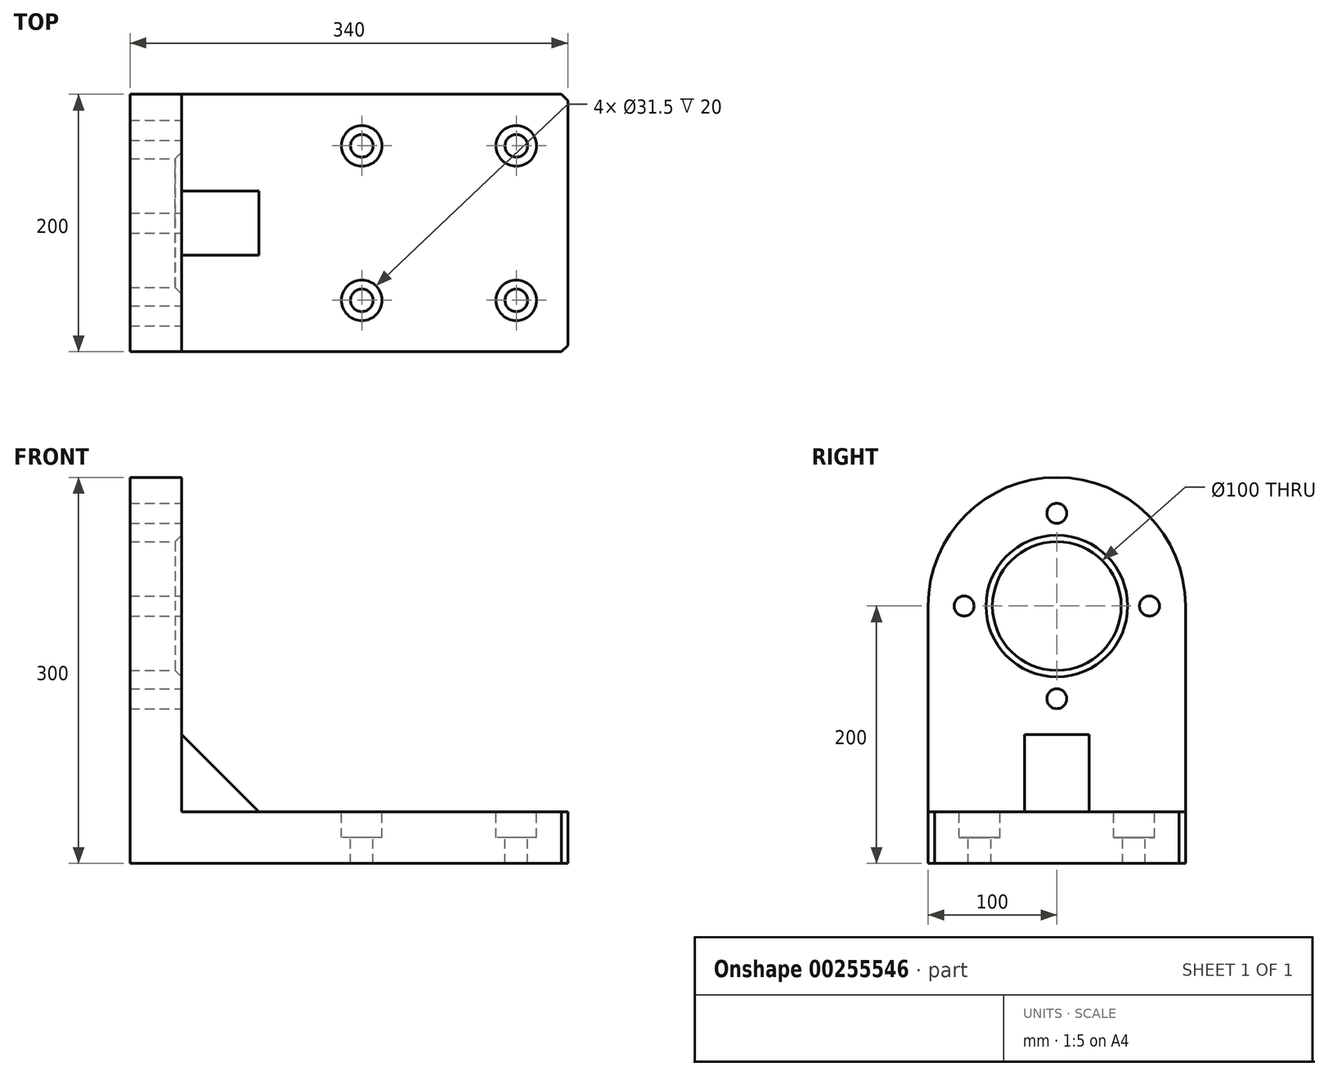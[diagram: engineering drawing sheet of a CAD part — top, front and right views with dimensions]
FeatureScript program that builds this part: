
annotation { "Feature Type Name" : "Feature", "Feature Type Description" : "" }
export const myFeature = defineFeature(function(context is Context, id is Id, definition is map)
    precondition{}
    {
        {
            var Q0;
            Q0=qCreatedBy(makeId("Top.planeOp"),FACE);
            var sketch = newSketch(context, id + "F0", { "sketchPlane" : qUnion([Q0])});
            skLineSegment(sketch, "E0.bottom", {"start": v(150, 100) * mm, "end": v(-150, 100) * mm});
            skLineSegment(sketch, "E0.top", {"start": v(150, -100) * mm, "end": v(-150, -100) * mm});
            skLineSegment(sketch, "E0.left", {"start": v(150, 100) * mm, "end": v(150, -100) * mm});
            skLineSegment(sketch, "E0.right", {"start": v(-150, 100) * mm, "end": v(-150, -100) * mm});
            skPoint(sketch, "E0.middle", {"position": v(0, 0) * mm});
            skCircle(sketch, "E1", {"center": v(-10, 60) * mm, "radius": 8.75 * mm});
            skCircle(sketch, "E2", {"center": v(110, 60) * mm, "radius": 8.75 * mm});
            skCircle(sketch, "E3", {"center": v(110, -60) * mm, "radius": 8.75 * mm});
            skCircle(sketch, "E4", {"center": v(-10, -60) * mm, "radius": 8.75 * mm});
            skCircle(sketch, "E5", {"center": v(-10, 60) * mm, "radius": 15.75 * mm});
            skCircle(sketch, "E6", {"center": v(110, 60) * mm, "radius": 15.75 * mm});
            skCircle(sketch, "E7", {"center": v(110, -60) * mm, "radius": 15.75 * mm});
            skCircle(sketch, "E8", {"center": v(-10, -60) * mm, "radius": 15.75 * mm});
            skSolve(sketch);
        }
        {
            var Q0;
            Q0 = qSketchRegion(id + "F0", true);
            var Q1;
            Q1=makeQuery(id+"F0.imprint","IMPRINT",FACE,{"disambiguationData":[TD([[makeQuery(id+"F0.imprint","IMPRINT",EDGE,{"derivedFrom":sQuery(id+"F0.wireOp",EDGE,"E1")}),-1.0]])]});
            var Q2;
            Q2=makeQuery(id+"F0.imprint","IMPRINT",FACE,{"disambiguationData":[TD([[makeQuery(id+"F0.imprint","IMPRINT",EDGE,{"derivedFrom":sQuery(id+"F0.wireOp",EDGE,"E2")}),-1.0]])]});
            var Q3;
            Q3=makeQuery(id+"F0.imprint","IMPRINT",FACE,{"disambiguationData":[TD([[makeQuery(id+"F0.imprint","IMPRINT",EDGE,{"derivedFrom":sQuery(id+"F0.wireOp",EDGE,"E4")}),-1.0]])]});
            var Q4;
            Q4=makeQuery(id+"F0.imprint","IMPRINT",FACE,{"disambiguationData":[TD([[makeQuery(id+"F0.imprint","IMPRINT",EDGE,{"derivedFrom":sQuery(id+"F0.wireOp",EDGE,"E3")}),-1.0]])]});
            extrude(context, id + "F1", {"entities" : qUnion([Q0, Q1, Q2, Q3, Q4]), "oppositeDirection" : true, "depth" : 40 * mm});
        }
        {
            var Q0;
            Q0=makeQuery(id+"F0.imprint","IMPRINT",FACE,{"disambiguationData":[TD([[makeQuery(id+"F0.imprint","IMPRINT",EDGE,{"derivedFrom":sQuery(id+"F0.wireOp",EDGE,"E1")}),-1.0]])]});
            var Q1;
            Q1=makeQuery(id+"F0.imprint","IMPRINT",FACE,{"disambiguationData":[TD([[makeQuery(id+"F0.imprint","IMPRINT",EDGE,{"derivedFrom":sQuery(id+"F0.wireOp",EDGE,"E2")}),-1.0]])]});
            var Q2;
            Q2=makeQuery(id+"F0.imprint","IMPRINT",FACE,{"disambiguationData":[TD([[makeQuery(id+"F0.imprint","IMPRINT",EDGE,{"derivedFrom":sQuery(id+"F0.wireOp",EDGE,"E3")}),-1.0]])]});
            var Q3;
            Q3=makeQuery(id+"F0.imprint","IMPRINT",FACE,{"disambiguationData":[TD([[makeQuery(id+"F0.imprint","IMPRINT",EDGE,{"derivedFrom":sQuery(id+"F0.wireOp",EDGE,"E4")}),-1.0]])]});
            extrude(context, id + "F2", {"entities" : qUnion([Q0, Q1, Q2, Q3]), "operationType" : NewBodyOperationType.REMOVE, "oppositeDirection" : true, "depth" : 20 * mm});
        }
        {
            var Q0;
            Q0=makeQuery(id+"F1.opExtrude","SWEPT_FACE",FACE,{"disambiguationData":[OSD([sQuery(id+"F0.wireOp",EDGE,"E0.right")])]});
            var sketch = newSketch(context, id + "F3", { "sketchPlane" : qUnion([Q0])});
            skLineSegment(sketch, "E9.bottom", {"start": v(-100, -40) * mm, "end": v(100, -40) * mm});
            skLineSegment(sketch, "E9.top", {"start": v(-100, 260) * mm, "end": v(100, 260) * mm, "construction": true});
            skLineSegment(sketch, "E9.left", {"start": v(-100, -40) * mm, "end": v(-100, 160) * mm});
            skLineSegment(sketch, "E9.right", {"start": v(100, -40) * mm, "end": v(100, 160) * mm});
            skCircle(sketch, "E10", {"center": v(0, 160) * mm, "radius": 100 * mm});
            skCircle(sketch, "E11", {"center": v(0, 160) * mm, "radius": 50 * mm});
            skCircle(sketch, "E12", {"center": v(0, 160) * mm, "radius": 72 * mm, "construction": true});
            skPoint(sketch, "E13", {"position": v(0, 232) * mm});
            skPoint(sketch, "E14", {"position": v(72, 160) * mm});
            skPoint(sketch, "E15", {"position": v(0, 88) * mm});
            skPoint(sketch, "E16", {"position": v(-72, 160) * mm});
            skSolve(sketch);
        }
        {
            var Q0;
            Q0 = qSketchRegion(id + "F3", true);
            extrude(context, id + "F4", {"entities" : qUnion([Q0]), "operationType" : NewBodyOperationType.ADD, "depth" : 40 * mm});
        }
        {
            var Q0;
            Q0=sQuery(id+"F3.wireOp",VERTEX,"E16");
            var Q1;
            Q1=sQuery(id+"F3.wireOp",VERTEX,"E13");
            var Q2;
            Q2=sQuery(id+"F3.wireOp",VERTEX,"E14");
            var Q3;
            Q3=sQuery(id+"F3.wireOp",VERTEX,"E15");
            var Q4;
            Q4=makeQuery(id+"F1.opExtrude","SWEPT_BODY",BODY,{"disambiguationData":[OSD([sQuery(id+"F0.wireOp",EDGE,"E0.bottom"),sQuery(id+"F0.wireOp",EDGE,"E0.top"),sQuery(id+"F0.wireOp",EDGE,"E0.left"),sQuery(id+"F0.wireOp",EDGE,"E0.right"),sQuery(id+"F0.wireOp",EDGE,"E1"),sQuery(id+"F0.wireOp",EDGE,"E2"),sQuery(id+"F0.wireOp",EDGE,"E4"),sQuery(id+"F0.wireOp",EDGE,"E3")])]});
            hole(context, id + "F5", {"style" : HoleStyle.SIMPLE, "endStyle" : HoleEndStyle.THROUGH, "oppositeDirection" : true, "standardTappedOrClearance" : lookupTablePath({ "standard" : "ISO", "fit" : "Normal", "size" : "M14", "type" : "Clearance" }), "standardBlindInLast" : lookupTablePath({ "fit" : "Standard", "standard" : "ISO", "size" : "M14", "type" : "Clearance" }), "holeDiameter" : 15.5 * mm, "tappedDepth" : 12.7 * mm, "tapClearance" : 3, "locations" : qUnion([Q0, Q1, Q2, Q3]), "scope" : qUnion([Q4])});
        }
        {
            var Q0;
            Q0=qCreatedBy(makeId("Front.planeOp"),FACE);
            var sketch = newSketch(context, id + "F6", { "sketchPlane" : qUnion([Q0])});
            skLineSegment(sketch, "E17.0", {"start": v(-150, 0) * mm, "end": v(-150, 160) * mm});
            skLineSegment(sketch, "E18.0", {"start": v(150, 0) * mm, "end": v(-150, 0) * mm});
            skLineSegment(sketch, "E19", {"start": v(-150, 60) * mm, "end": v(-90, 0) * mm});
            skSolve(sketch);
        }
        {
            var Q0;
            Q0 = qSketchRegion(id + "F6", true);
            extrude(context, id + "F7", {"entities" : qUnion([Q0]), "operationType" : NewBodyOperationType.ADD, "endBound" : BoundingType.SYMMETRIC, "depth" : 50 * mm});
        }
        {
            var Q0;
            Q0=makeQuery(id+"F1.opExtrude","SWEPT_EDGE",EDGE,{"disambiguationData":[OSD([sQuery(id+"F0.wireOp",EDGE,"E0.top"),sQuery(id+"F0.wireOp",EDGE,"E0.left")])]});
            var Q1;
            Q1=makeQuery(id+"F1.opExtrude","SWEPT_EDGE",EDGE,{"disambiguationData":[OSD([sQuery(id+"F0.wireOp",EDGE,"E0.bottom"),sQuery(id+"F0.wireOp",EDGE,"E0.left")])]});
            var Q2;
            Q2=makeQuery(id+"F4.opExtrude","CAP_EDGE",EDGE,{"disambiguationData":[OSD([sQuery(id+"F3.wireOp",EDGE,"E11")])],"isStart":true});
            chamfer(context, id + "F8", {"entities" : qUnion([Q0, Q1, Q2]), "width" : 5 * mm, "tangentPropagation" : true});
        }
    });
